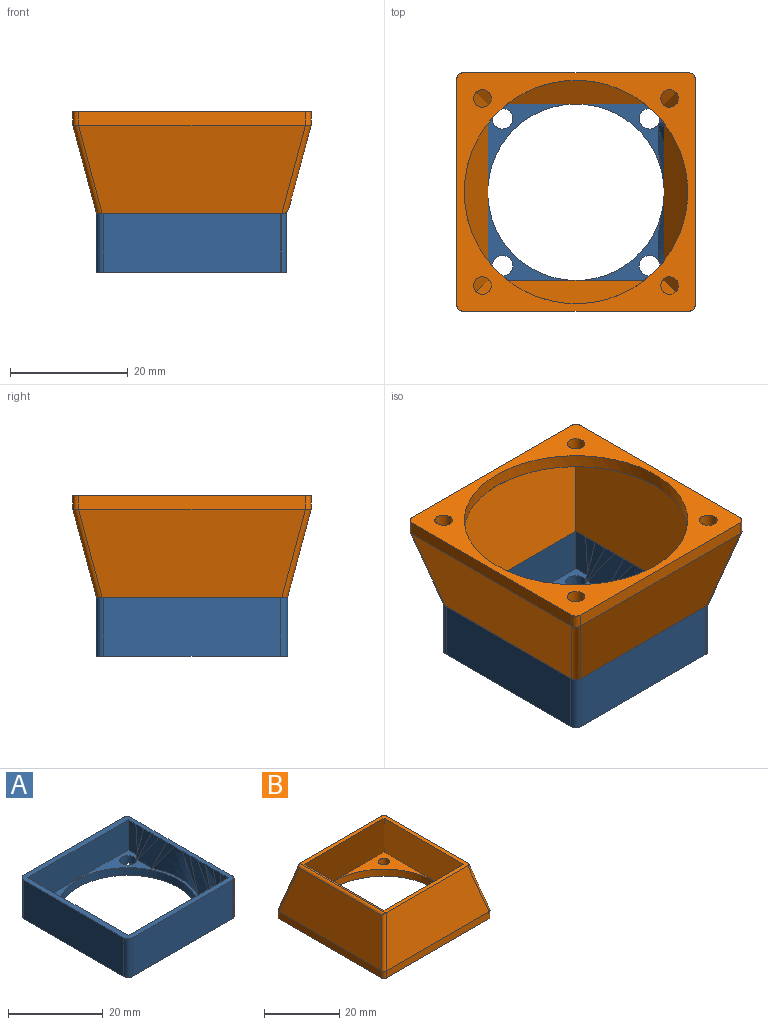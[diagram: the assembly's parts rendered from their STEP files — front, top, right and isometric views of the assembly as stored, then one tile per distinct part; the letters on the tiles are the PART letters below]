
ASSEMBLY  parts=2 mates=1
PART A: 49 faces, bbox 32.3x32.5x10 mm
  f0: plane 4.23x2mm, normal (1,0,0), area 8.5mm2, adj f1,f12,f13,f19
  f1: cylinder r=16mm len=13.95mm, axis (0,0,-1), area 28.9mm2, adj f0,f2,f12,f18
  f2: plane 4.23x2mm, normal (1,0,0), area 8.5mm2, adj f1,f12,f14,f17
  f3: plane 2x0.8mm, normal (0,-1,0), area 1.6mm2, adj f4,f12,f14,f15
  f4: plane 10x3mm, normal (1,0,0), area 28.2mm2, adj f3,f12,f15,f22,f47
  f5: plane 10x3mm, normal (1,0,0), area 28.2mm2, adj f10,f12,f21,f22,f48
  f6: cylinder r=1.75mm len=3.5mm, axis (0,0,-1), area 22mm2, adj f12,f23
  f7: cylinder r=1.75mm len=3.5mm, axis (0,0,-1), area 22mm2, adj f12,f23
  f8: cylinder r=15mm len=30mm, axis (0,0,-1), area 188.5mm2, adj f12,f23
  f9: cylinder r=1.75mm len=3.5mm, axis (0,0,-1), area 22mm2, adj f12,f23
  f10: plane 2x0.8mm, normal (0,1,0), area 1.6mm2, adj f5,f12,f13,f21
  f11: cylinder r=1.75mm len=3.5mm, axis (0,0,-1), area 22mm2, adj f12,f23
  f12: plane 32.5x32.28mm, normal (0,0,-1), area 278.9mm2, adj f0,f1,f2,f3,f4,f5,f6,f7
  f13: cylinder r=1.51mm len=2mm, axis (0,0,1), area 2.3mm2, adj f0,f10,f12,f20
  f14: cylinder r=1.51mm len=2mm, axis (0,0,1), area 2.3mm2, adj f2,f3,f12,f16
  f15: bspline ~8x3.56mm, area 15.4mm2, adj f3,f4,f16,f22
  f16: bspline ~8x6.67mm, area 18.7mm2, adj f14,f15,f17,f22
  f17: plane 9.42x8mm, normal (0.98,0,-0.2), area 31.7mm2, adj f2,f16,f18,f22
  f18: bspline ~13.95x8mm, area 71.7mm2, adj f1,f17,f19,f22
  f19: plane 9.42x8mm, normal (0.98,0,-0.2), area 31.7mm2, adj f0,f18,f20,f22
  f20: bspline ~8x6.67mm, area 18.7mm2, adj f13,f19,f21,f22
  f21: bspline ~8x3.56mm, area 15.4mm2, adj f5,f10,f20,f22
  f22: plane 32.5x32.28mm, normal (0,0,1), area 147.1mm2, adj f4,f5,f15,f16,f17,f18,f19,f20
  f23: plane 30.8x30.4mm, normal (0,0,1), area 164.8mm2, adj f6,f7,f8,f9,f11,f24,f25,f26
  f24: plane 8x2.83mm, normal (-1,0,-0.02), area 20.6mm2, adj f22,f23,f25,f39
  f25: bspline ~8x2.31mm, area 9.3mm2, adj f22,f23,f24,f26
  f26: bspline ~8x4.29mm, area 14.5mm2, adj f22,f23,f25,f27
  f27: bspline ~8x5.59mm, area 9.9mm2, adj f22,f23,f26,f28
  f28: plane 8x7.74mm, normal (-0.99,0,0.12), area 26.3mm2, adj f22,f23,f27,f29
  f29: bspline ~8x5.82mm, area 10mm2, adj f22,f23,f28,f30
  f30: bspline ~13.6x8mm, area 65.7mm2, adj f22,f23,f29,f31
  f31: bspline ~8x5.82mm, area 10mm2, adj f22,f23,f30,f32
  f32: plane 8x7.74mm, normal (-0.99,0,0.12), area 26.3mm2, adj f22,f23,f31,f33
  f33: bspline ~8x5.59mm, area 9.9mm2, adj f22,f23,f32,f34
  f34: bspline ~8x4.29mm, area 14.5mm2, adj f22,f23,f33,f35
  f35: bspline ~8x2.31mm, area 9.3mm2, adj f22,f23,f34,f36
  f36: plane 8x2.83mm, normal (-1,0,-0.02), area 20.6mm2, adj f22,f23,f35,f37
  f37: plane 30.4x8mm, normal (0,1,-0.02), area 241.7mm2, adj f22,f23,f36,f38
  f38: plane 30.4x8mm, normal (1,0,-0.02), area 241.7mm2, adj f22,f23,f37,f39
  f39: plane 30.4x8mm, normal (0,-1,-0.02), area 241.7mm2, adj f22,f23,f24,f38
  f40: cylinder r=1.25mm len=10mm, axis (0,0,-1), area 1.6mm2, adj f12,f22,f43,f47
  f41: cylinder r=1.25mm len=10mm, axis (0,0,1), area 1.6mm2, adj f12,f22,f46,f48
  f42: cylinder r=1.25mm len=10mm, axis (0,0,1), area 19.6mm2, adj f12,f22,f43,f44
  f43: plane 30x10mm, normal (0,1,0), area 300mm2, adj f12,f22,f40,f42
  f44: plane 30x10mm, normal (-1,0,0), area 300mm2, adj f12,f22,f42,f45
  f45: cylinder r=1.25mm len=10mm, axis (0,0,-1), area 19.6mm2, adj f12,f22,f44,f46
  f46: plane 30x10mm, normal (0,-1,0), area 300mm2, adj f12,f22,f41,f45
  f47: cylinder r=1mm len=10mm, axis (0,0,-1), area 17mm2, adj f4,f12,f22,f40
  f48: cylinder r=1mm len=10mm, axis (0,0,1), area 17mm2, adj f5,f12,f22,f41
PART B: 32 faces, bbox 40.5x40.5x17.4 mm
  f0: plane 32.47x31.71mm, normal (0,0,1), area 129mm2, adj f1,f2,f4,f5,f6,f7,f8,f23
  f1: plane 38.57x15mm, normal (0.97,0,0.26), area 536.5mm2, adj f0,f14,f23,f24,f25,f26
  f2: plane 38.57x15mm, normal (0,0.97,0.26), area 536.5mm2, adj f0,f15,f25,f26,f30,f31
  f3: plane 38.57x14.26mm, normal (-0.97,0,0.26), area 512.9mm2, adj f16,f27,f28,f29,f30,f31
  f4: plane 38.57x15mm, normal (0,-0.97,0.26), area 536.5mm2, adj f0,f13,f23,f24,f27,f28
  f5: plane 38x15mm, normal (0,-0.97,-0.26), area 527.8mm2, adj f0,f6,f8,f10,f11
  f6: plane 38x15mm, normal (0.97,0,-0.26), area 527.8mm2, adj f0,f5,f7,f11,f12
  f7: plane 38x15mm, normal (0,0.97,-0.26), area 527.8mm2, adj f0,f6,f8,f9,f12
  f8: plane 38x15mm, normal (-0.97,0,-0.26), area 527.8mm2, adj f0,f5,f7,f9,f10
  f9: plane 19x19mm, normal (0,0,1), area 70.4mm2, adj f7,f8,f20,f21
  f10: plane 19x19mm, normal (0,0,1), area 70.4mm2, adj f5,f8,f17,f20
  f11: plane 19x19mm, normal (0,0,1), area 70.4mm2, adj f5,f6,f18,f20
  f12: plane 19x19mm, normal (0,0,1), area 70.4mm2, adj f6,f7,f19,f20
  f13: plane 38.5x2.3mm, normal (0,-1,0), area 88.5mm2, adj f4,f22,f24,f27
  f14: plane 38.5x2.3mm, normal (1,0,0), area 88.5mm2, adj f1,f22,f24,f26
  f15: plane 38.5x2.3mm, normal (0,1,0), area 88.5mm2, adj f2,f22,f26,f31
  f16: plane 38.5x2.3mm, normal (-1,0,0), area 88.5mm2, adj f3,f22,f27,f31
  f17: cylinder r=1.5mm len=3mm, axis (0,0,1), area 21.7mm2, adj f10,f22
  f18: cylinder r=1.5mm len=3mm, axis (0,0,1), area 21.7mm2, adj f11,f22
  f19: cylinder r=1.5mm len=3mm, axis (0,0,1), area 21.7mm2, adj f12,f22
  f20: cylinder r=19mm len=38mm, axis (0,0,1), area 274.6mm2, adj f9,f10,f11,f12,f22
  f21: cylinder r=1.5mm len=3mm, axis (0,0,1), area 21.7mm2, adj f9,f22
  f22: plane 40.5x40.5mm, normal (0,0,-1), area 477mm2, adj f13,f14,f15,f16,f17,f18,f19,f20
  f23: cylinder r=1mm len=15.14mm, axis (0.25,-0.25,-0.94), area 24.1mm2, adj f0,f1,f4,f24
  f24: cylinder r=1mm len=2.35mm, axis (0,0,-1), area 3.7mm2, adj f1,f4,f13,f14,f22,f23
  f25: cylinder r=1mm len=15.14mm, axis (-0.25,-0.25,0.94), area 24.1mm2, adj f0,f1,f2,f26
  f26: cylinder r=1mm len=2.35mm, axis (0,0,1), area 3.7mm2, adj f1,f2,f14,f15,f22,f25
  f27: cylinder r=1mm len=2.35mm, axis (0,0,1), area 3.7mm2, adj f3,f4,f13,f16,f22,f28
  f28: cylinder r=1mm len=15.14mm, axis (0.25,0.25,0.94), area 23.7mm2, adj f0,f3,f4,f27,f29
  f29: cylinder r=1mm len=32.43mm, axis (0,1,0), area 41.7mm2, adj f0,f3,f28,f30
  f30: cylinder r=1mm len=15.14mm, axis (-0.25,0.25,-0.94), area 23.7mm2, adj f0,f2,f3,f29,f31
  f31: cylinder r=1mm len=2.35mm, axis (0,0,-1), area 3.7mm2, adj f2,f3,f15,f16,f22,f30
PLACE A rot(axis=(0,1,0),0deg) t=(-0.22,0.22,0)mm
PLACE B rot(axis=(0,1,0),180deg) t=(-0.22,0.22,25)mm
MATE fastened A.f41 <-> B.f0  axis (0,0,1) through (14.78,-14.78,10)mm
